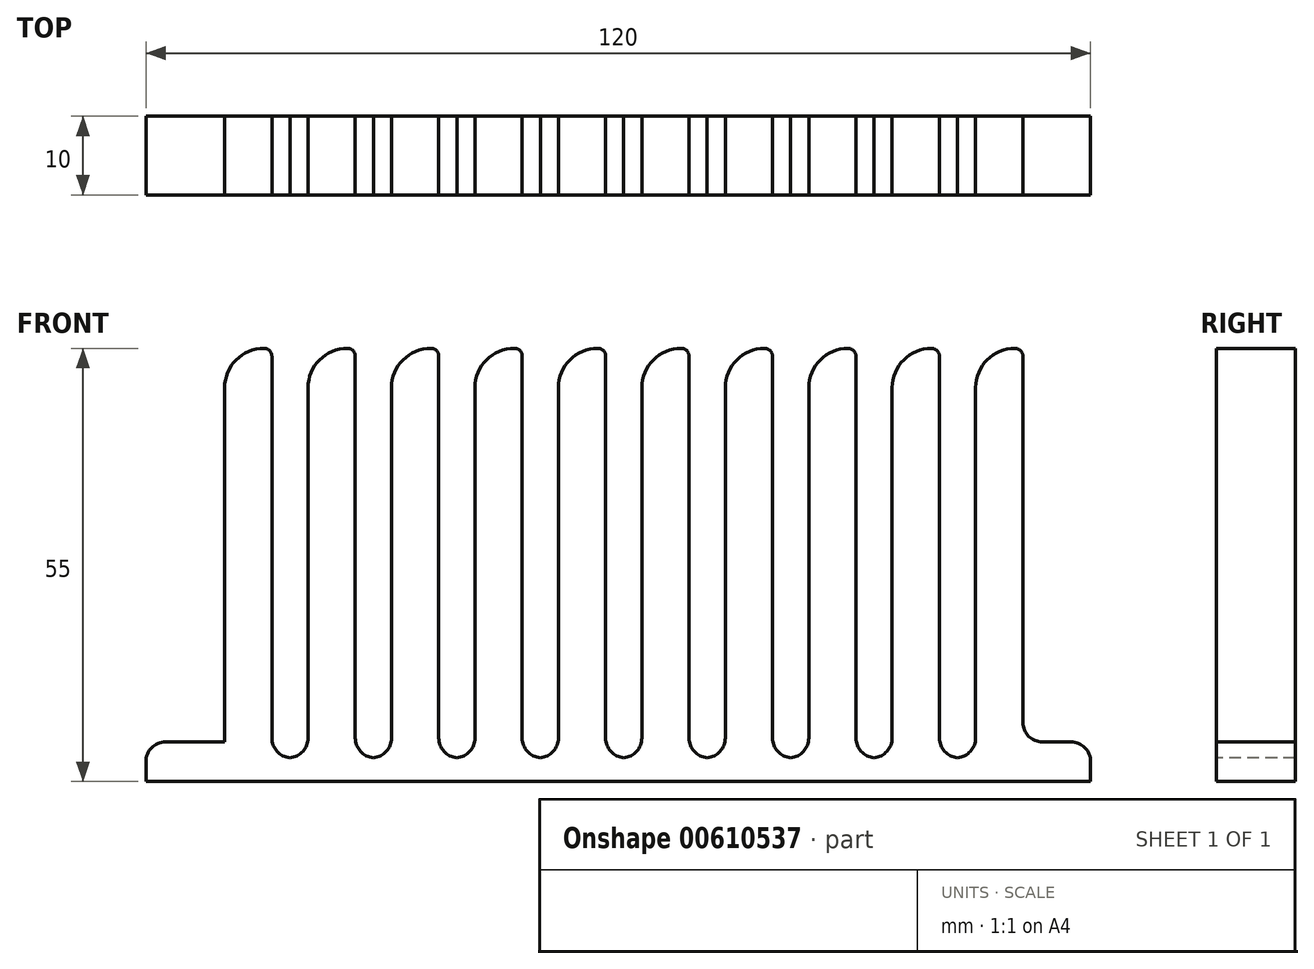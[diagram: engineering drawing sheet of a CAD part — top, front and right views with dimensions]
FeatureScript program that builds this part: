
annotation { "Feature Type Name" : "Feature", "Feature Type Description" : "" }
export const myFeature = defineFeature(function(context is Context, id is Id, definition is map)
    precondition{}
    {
        {
            var Q0;
            Q0=qCreatedBy(makeId("Top.planeOp"),FACE);
            var sketch = newSketch(context, id + "F0", { "sketchPlane" : qUnion([Q0])});
            skLineSegment(sketch, "E0.bottom", {"start": v(-61.1, -50) * mm, "end": v(58.9, -50) * mm});
            skLineSegment(sketch, "E0.top", {"start": v(-61.1, -60) * mm, "end": v(58.9, -60) * mm});
            skLineSegment(sketch, "E0.left", {"start": v(-61.1, -50) * mm, "end": v(-61.1, -60) * mm});
            skLineSegment(sketch, "E0.right", {"start": v(58.9, -50) * mm, "end": v(58.9, -60) * mm});
            skSolve(sketch);
        }
        {
            var Q0;
            Q0 = qSketchRegion(id + "F0", true);
            extrude(context, id + "F1", {"entities" : qUnion([Q0]), "depth" : 5 * mm, "offsetDistance" : 25 * mm});
        }
        {
            var Q0;
            Q0=makeQuery(id+"F1.opExtrude","CAP_FACE",FACE,{"disambiguationData":[OSD([sQuery(id+"F0.wireOp",EDGE,"E0.bottom"),sQuery(id+"F0.wireOp",EDGE,"E0.top"),sQuery(id+"F0.wireOp",EDGE,"E0.left"),sQuery(id+"F0.wireOp",EDGE,"E0.right")])],"isStart":false});
            var sketch = newSketch(context, id + "F2", { "sketchPlane" : qUnion([Q0])});
            skLineSegment(sketch, "E1.bottom", {"start": v(-51.1, -50) * mm, "end": v(-45.1, -50) * mm});
            skLineSegment(sketch, "E1.top", {"start": v(-51.1, -60) * mm, "end": v(-45.1, -60) * mm});
            skLineSegment(sketch, "E1.left", {"start": v(-51.1, -50) * mm, "end": v(-51.1, -60) * mm});
            skLineSegment(sketch, "E1.right", {"start": v(-45.1, -50) * mm, "end": v(-45.1, -60) * mm});
            skLineSegment(sketch, "E2.1.0.0", {"start": v(-34.5, -50) * mm, "end": v(-34.5, -60) * mm});
            skLineSegment(sketch, "E2.1.0.1", {"start": v(-40.5, -50) * mm, "end": v(-34.5, -50) * mm});
            skLineSegment(sketch, "E2.1.0.2", {"start": v(-40.5, -60) * mm, "end": v(-34.5, -60) * mm});
            skLineSegment(sketch, "E2.1.0.3", {"start": v(-40.5, -50) * mm, "end": v(-40.5, -60) * mm});
            skLineSegment(sketch, "E2.2.0.0", {"start": v(-23.9, -50) * mm, "end": v(-23.9, -60) * mm});
            skLineSegment(sketch, "E2.2.0.1", {"start": v(-29.9, -50) * mm, "end": v(-23.9, -50) * mm});
            skLineSegment(sketch, "E2.2.0.2", {"start": v(-29.9, -60) * mm, "end": v(-23.9, -60) * mm});
            skLineSegment(sketch, "E2.2.0.3", {"start": v(-29.9, -50) * mm, "end": v(-29.9, -60) * mm});
            skLineSegment(sketch, "E2.3.0.0", {"start": v(-13.3, -50) * mm, "end": v(-13.3, -60) * mm});
            skLineSegment(sketch, "E2.3.0.1", {"start": v(-19.3, -50) * mm, "end": v(-13.3, -50) * mm});
            skLineSegment(sketch, "E2.3.0.2", {"start": v(-19.3, -60) * mm, "end": v(-13.3, -60) * mm});
            skLineSegment(sketch, "E2.3.0.3", {"start": v(-19.3, -50) * mm, "end": v(-19.3, -60) * mm});
            skLineSegment(sketch, "E2.4.0.0", {"start": v(-2.7, -50) * mm, "end": v(-2.7, -60) * mm});
            skLineSegment(sketch, "E2.4.0.1", {"start": v(-8.7, -50) * mm, "end": v(-2.7, -50) * mm});
            skLineSegment(sketch, "E2.4.0.2", {"start": v(-8.7, -60) * mm, "end": v(-2.7, -60) * mm});
            skLineSegment(sketch, "E2.4.0.3", {"start": v(-8.7, -50) * mm, "end": v(-8.7, -60) * mm});
            skLineSegment(sketch, "E2.5.0.0", {"start": v(7.9, -50) * mm, "end": v(7.9, -60) * mm});
            skLineSegment(sketch, "E2.5.0.1", {"start": v(1.9, -50) * mm, "end": v(7.9, -50) * mm});
            skLineSegment(sketch, "E2.5.0.2", {"start": v(1.9, -60) * mm, "end": v(7.9, -60) * mm});
            skLineSegment(sketch, "E2.5.0.3", {"start": v(1.9, -50) * mm, "end": v(1.9, -60) * mm});
            skLineSegment(sketch, "E2.6.0.0", {"start": v(18.5, -50) * mm, "end": v(18.5, -60) * mm});
            skLineSegment(sketch, "E2.6.0.1", {"start": v(12.5, -50) * mm, "end": v(18.5, -50) * mm});
            skLineSegment(sketch, "E2.6.0.2", {"start": v(12.5, -60) * mm, "end": v(18.5, -60) * mm});
            skLineSegment(sketch, "E2.6.0.3", {"start": v(12.5, -50) * mm, "end": v(12.5, -60) * mm});
            skLineSegment(sketch, "E2.7.0.0", {"start": v(29.1, -50) * mm, "end": v(29.1, -60) * mm});
            skLineSegment(sketch, "E2.7.0.1", {"start": v(23.1, -50) * mm, "end": v(29.1, -50) * mm});
            skLineSegment(sketch, "E2.7.0.2", {"start": v(23.1, -60) * mm, "end": v(29.1, -60) * mm});
            skLineSegment(sketch, "E2.7.0.3", {"start": v(23.1, -50) * mm, "end": v(23.1, -60) * mm});
            skLineSegment(sketch, "E2.8.0.0", {"start": v(39.7, -50) * mm, "end": v(39.7, -60) * mm});
            skLineSegment(sketch, "E2.8.0.1", {"start": v(33.7, -50) * mm, "end": v(39.7, -50) * mm});
            skLineSegment(sketch, "E2.8.0.2", {"start": v(33.7, -60) * mm, "end": v(39.7, -60) * mm});
            skLineSegment(sketch, "E2.8.0.3", {"start": v(33.7, -50) * mm, "end": v(33.7, -60) * mm});
            skLineSegment(sketch, "E2.9.0.0", {"start": v(50.3, -50) * mm, "end": v(50.3, -60) * mm});
            skLineSegment(sketch, "E2.9.0.1", {"start": v(44.3, -50) * mm, "end": v(50.3, -50) * mm});
            skLineSegment(sketch, "E2.9.0.2", {"start": v(44.3, -60) * mm, "end": v(50.3, -60) * mm});
            skLineSegment(sketch, "E2.9.0.3", {"start": v(44.3, -50) * mm, "end": v(44.3, -60) * mm});
            skLineSegment(sketch, "E2.direction1", {"start": v(-51.1, -60) * mm, "end": v(-40.5, -60) * mm, "construction": true});
            skSolve(sketch);
        }
        {
            var Q0;
            Q0 = qSketchRegion(id + "F2", true);
            extrude(context, id + "F3", {"entities" : qUnion([Q0]), "operationType" : NewBodyOperationType.ADD, "depth" : 50 * mm, "offsetDistance" : 25 * mm});
        }
        {
            var Q0;
            {var subQ0=sQuery(id+"F0.wireOp",EDGE,"E0.top");var subQ1=sQuery(id+"F0.wireOp",EDGE,"E0.bottom");Q0=makeQuery(id+"F3.boolean.opBoolean","SPLIT",FACE,{"disambiguationData":[TD([makeQuery(id+"F3.opExtrude","SWEPT_FACE",FACE,{"disambiguationData":[OSD([sQuery(id+"F2.wireOp",EDGE,"E1.right")])]})])],"derivedFrom":makeQuery(id+"F1.opExtrude","CAP_FACE",FACE,{"disambiguationData":[OSD([subQ1,subQ0,sQuery(id+"F0.wireOp",EDGE,"E0.left"),sQuery(id+"F0.wireOp",EDGE,"E0.right")])],"isStart":false})});}
            var sketch = newSketch(context, id + "F4", { "sketchPlane" : qUnion([Q0])});
            skLineSegment(sketch, "E3.bottom", {"start": v(-45.1, -50) * mm, "end": v(-40.5, -50) * mm});
            skLineSegment(sketch, "E3.top", {"start": v(-45.1, -60) * mm, "end": v(-40.5, -60) * mm});
            skLineSegment(sketch, "E3.left", {"start": v(-45.1, -50) * mm, "end": v(-45.1, -60) * mm});
            skLineSegment(sketch, "E3.right", {"start": v(-40.5, -50) * mm, "end": v(-40.5, -60) * mm});
            skLineSegment(sketch, "E4.1.0.0", {"start": v(-34.5, -60) * mm, "end": v(-29.9, -60) * mm});
            skLineSegment(sketch, "E4.1.0.1", {"start": v(-34.5, -50) * mm, "end": v(-34.5, -60) * mm});
            skLineSegment(sketch, "E4.1.0.2", {"start": v(-29.9, -50) * mm, "end": v(-29.9, -60) * mm});
            skLineSegment(sketch, "E4.1.0.3", {"start": v(-34.5, -50) * mm, "end": v(-29.9, -50) * mm});
            skLineSegment(sketch, "E4.2.0.0", {"start": v(-23.9, -60) * mm, "end": v(-19.3, -60) * mm});
            skLineSegment(sketch, "E4.2.0.1", {"start": v(-23.9, -50) * mm, "end": v(-23.9, -60) * mm});
            skLineSegment(sketch, "E4.2.0.2", {"start": v(-19.3, -50) * mm, "end": v(-19.3, -60) * mm});
            skLineSegment(sketch, "E4.2.0.3", {"start": v(-23.9, -50) * mm, "end": v(-19.3, -50) * mm});
            skLineSegment(sketch, "E4.3.0.0", {"start": v(-13.3, -60) * mm, "end": v(-8.7, -60) * mm});
            skLineSegment(sketch, "E4.3.0.1", {"start": v(-13.3, -50) * mm, "end": v(-13.3, -60) * mm});
            skLineSegment(sketch, "E4.3.0.2", {"start": v(-8.7, -50) * mm, "end": v(-8.7, -60) * mm});
            skLineSegment(sketch, "E4.3.0.3", {"start": v(-13.3, -50) * mm, "end": v(-8.7, -50) * mm});
            skLineSegment(sketch, "E4.4.0.0", {"start": v(-2.7, -60) * mm, "end": v(1.9, -60) * mm});
            skLineSegment(sketch, "E4.4.0.1", {"start": v(-2.7, -50) * mm, "end": v(-2.7, -60) * mm});
            skLineSegment(sketch, "E4.4.0.2", {"start": v(1.9, -50) * mm, "end": v(1.9, -60) * mm});
            skLineSegment(sketch, "E4.4.0.3", {"start": v(-2.7, -50) * mm, "end": v(1.9, -50) * mm});
            skLineSegment(sketch, "E4.5.0.0", {"start": v(7.9, -60) * mm, "end": v(12.5, -60) * mm});
            skLineSegment(sketch, "E4.5.0.1", {"start": v(7.9, -50) * mm, "end": v(7.9, -60) * mm});
            skLineSegment(sketch, "E4.5.0.2", {"start": v(12.5, -50) * mm, "end": v(12.5, -60) * mm});
            skLineSegment(sketch, "E4.5.0.3", {"start": v(7.9, -50) * mm, "end": v(12.5, -50) * mm});
            skLineSegment(sketch, "E4.6.0.0", {"start": v(18.5, -60) * mm, "end": v(23.1, -60) * mm});
            skLineSegment(sketch, "E4.6.0.1", {"start": v(18.5, -50) * mm, "end": v(18.5, -60) * mm});
            skLineSegment(sketch, "E4.6.0.2", {"start": v(23.1, -50) * mm, "end": v(23.1, -60) * mm});
            skLineSegment(sketch, "E4.6.0.3", {"start": v(18.5, -50) * mm, "end": v(23.1, -50) * mm});
            skLineSegment(sketch, "E4.7.0.0", {"start": v(29.1, -60) * mm, "end": v(33.7, -60) * mm});
            skLineSegment(sketch, "E4.7.0.1", {"start": v(29.1, -50) * mm, "end": v(29.1, -60) * mm});
            skLineSegment(sketch, "E4.7.0.2", {"start": v(33.7, -50) * mm, "end": v(33.7, -60) * mm});
            skLineSegment(sketch, "E4.7.0.3", {"start": v(29.1, -50) * mm, "end": v(33.7, -50) * mm});
            skLineSegment(sketch, "E4.8.0.0", {"start": v(39.7, -60) * mm, "end": v(44.3, -60) * mm});
            skLineSegment(sketch, "E4.8.0.1", {"start": v(39.7, -50) * mm, "end": v(39.7, -60) * mm});
            skLineSegment(sketch, "E4.8.0.2", {"start": v(44.3, -50) * mm, "end": v(44.3, -60) * mm});
            skLineSegment(sketch, "E4.8.0.3", {"start": v(39.7, -50) * mm, "end": v(44.3, -50) * mm});
            skLineSegment(sketch, "E4.direction1", {"start": v(-45.1, -60) * mm, "end": v(-34.5, -60) * mm, "construction": true});
            skSolve(sketch);
        }
        {
            var Q0;
            Q0 = qSketchRegion(id + "F4", true);
            extrude(context, id + "F5", {"entities" : qUnion([Q0]), "operationType" : NewBodyOperationType.REMOVE, "oppositeDirection" : true, "depth" : 2 * mm, "offsetDistance" : 25 * mm});
        }
        {
            var Q0;
            Q0=makeQuery(id+"F5.boolean.opBoolean","COPY",EDGE,{"derivedFrom":makeQuery(id+"F5.opExtrude","CAP_EDGE",EDGE,{"disambiguationData":[OSD([sQuery(id+"F4.wireOp",EDGE,"E3.left")])],"isStart":false})});
            var Q1;
            Q1=makeQuery(id+"F5.boolean.opBoolean","COPY",EDGE,{"derivedFrom":makeQuery(id+"F5.opExtrude","CAP_EDGE",EDGE,{"disambiguationData":[OSD([sQuery(id+"F4.wireOp",EDGE,"E3.right")])],"isStart":false})});
            var Q2;
            Q2=makeQuery(id+"F5.boolean.opBoolean","COPY",EDGE,{"derivedFrom":makeQuery(id+"F5.opExtrude","CAP_EDGE",EDGE,{"disambiguationData":[OSD([sQuery(id+"F4.wireOp",EDGE,"E4.1.0.2")])],"isStart":false})});
            var Q3;
            Q3=makeQuery(id+"F5.boolean.opBoolean","COPY",EDGE,{"derivedFrom":makeQuery(id+"F5.opExtrude","CAP_EDGE",EDGE,{"disambiguationData":[OSD([sQuery(id+"F4.wireOp",EDGE,"E4.2.0.1")])],"isStart":false})});
            var Q4;
            Q4=makeQuery(id+"F5.boolean.opBoolean","COPY",EDGE,{"derivedFrom":makeQuery(id+"F5.opExtrude","CAP_EDGE",EDGE,{"disambiguationData":[OSD([sQuery(id+"F4.wireOp",EDGE,"E4.2.0.2")])],"isStart":false})});
            var Q5;
            Q5=makeQuery(id+"F5.boolean.opBoolean","COPY",EDGE,{"derivedFrom":makeQuery(id+"F5.opExtrude","CAP_EDGE",EDGE,{"disambiguationData":[OSD([sQuery(id+"F4.wireOp",EDGE,"E4.3.0.1")])],"isStart":false})});
            var Q6;
            Q6=makeQuery(id+"F5.boolean.opBoolean","COPY",EDGE,{"derivedFrom":makeQuery(id+"F5.opExtrude","CAP_EDGE",EDGE,{"disambiguationData":[OSD([sQuery(id+"F4.wireOp",EDGE,"E4.3.0.2")])],"isStart":false})});
            var Q7;
            Q7=makeQuery(id+"F5.boolean.opBoolean","COPY",EDGE,{"derivedFrom":makeQuery(id+"F5.opExtrude","CAP_EDGE",EDGE,{"disambiguationData":[OSD([sQuery(id+"F4.wireOp",EDGE,"E4.4.0.1")])],"isStart":false})});
            var Q8;
            Q8=makeQuery(id+"F5.boolean.opBoolean","COPY",EDGE,{"derivedFrom":makeQuery(id+"F5.opExtrude","CAP_EDGE",EDGE,{"disambiguationData":[OSD([sQuery(id+"F4.wireOp",EDGE,"E4.4.0.2")])],"isStart":false})});
            var Q9;
            Q9=makeQuery(id+"F5.boolean.opBoolean","COPY",EDGE,{"derivedFrom":makeQuery(id+"F5.opExtrude","CAP_EDGE",EDGE,{"disambiguationData":[OSD([sQuery(id+"F4.wireOp",EDGE,"E4.5.0.2")])],"isStart":false})});
            var Q10;
            Q10=makeQuery(id+"F5.boolean.opBoolean","COPY",EDGE,{"derivedFrom":makeQuery(id+"F5.opExtrude","CAP_EDGE",EDGE,{"disambiguationData":[OSD([sQuery(id+"F4.wireOp",EDGE,"E4.6.0.2")])],"isStart":false})});
            var Q11;
            Q11=makeQuery(id+"F5.boolean.opBoolean","COPY",EDGE,{"derivedFrom":makeQuery(id+"F5.opExtrude","CAP_EDGE",EDGE,{"disambiguationData":[OSD([sQuery(id+"F4.wireOp",EDGE,"E4.7.0.2")])],"isStart":false})});
            var Q12;
            Q12=makeQuery(id+"F5.boolean.opBoolean","COPY",EDGE,{"derivedFrom":makeQuery(id+"F5.opExtrude","CAP_EDGE",EDGE,{"disambiguationData":[OSD([sQuery(id+"F4.wireOp",EDGE,"E4.8.0.2")])],"isStart":false})});
            var Q13;
            Q13=makeQuery(id+"F5.boolean.opBoolean","COPY",EDGE,{"derivedFrom":makeQuery(id+"F5.opExtrude","CAP_EDGE",EDGE,{"disambiguationData":[OSD([sQuery(id+"F4.wireOp",EDGE,"E4.8.0.1")])],"isStart":false})});
            var Q14;
            Q14=makeQuery(id+"F5.boolean.opBoolean","COPY",EDGE,{"derivedFrom":makeQuery(id+"F5.opExtrude","CAP_EDGE",EDGE,{"disambiguationData":[OSD([sQuery(id+"F4.wireOp",EDGE,"E4.7.0.1")])],"isStart":false})});
            var Q15;
            Q15=makeQuery(id+"F5.boolean.opBoolean","COPY",EDGE,{"derivedFrom":makeQuery(id+"F5.opExtrude","CAP_EDGE",EDGE,{"disambiguationData":[OSD([sQuery(id+"F4.wireOp",EDGE,"E4.6.0.1")])],"isStart":false})});
            var Q16;
            Q16=makeQuery(id+"F5.boolean.opBoolean","COPY",EDGE,{"derivedFrom":makeQuery(id+"F5.opExtrude","CAP_EDGE",EDGE,{"disambiguationData":[OSD([sQuery(id+"F4.wireOp",EDGE,"E4.5.0.1")])],"isStart":false})});
            var Q17;
            Q17=makeQuery(id+"F3.opExtrude","CAP_EDGE",EDGE,{"disambiguationData":[OSD([sQuery(id+"F2.wireOp",EDGE,"E2.9.0.0")])],"isStart":true});
            var Q18;
            Q18=makeQuery(id+"F3.opExtrude","CAP_EDGE",EDGE,{"disambiguationData":[OSD([sQuery(id+"F2.wireOp",EDGE,"E1.left")])],"isStart":true});
            var Q19;
            Q19=makeQuery(id+"F5.boolean.opBoolean","COPY",EDGE,{"derivedFrom":makeQuery(id+"F5.opExtrude","CAP_EDGE",EDGE,{"disambiguationData":[OSD([sQuery(id+"F4.wireOp",EDGE,"E4.1.0.1")])],"isStart":false})});
            var Q20;
            Q20=makeQuery(id+"F1.opExtrude","CAP_EDGE",EDGE,{"disambiguationData":[OSD([sQuery(id+"F0.wireOp",EDGE,"E0.right")])],"isStart":false});
            var Q21;
            Q21=makeQuery(id+"F1.opExtrude","CAP_EDGE",EDGE,{"disambiguationData":[OSD([sQuery(id+"F0.wireOp",EDGE,"E0.left")])],"isStart":false});
            fillet(context, id + "F6", {"entities" : qUnion([Q0, Q1, Q2, Q3, Q4, Q5, Q6, Q7, Q8, Q9, Q10, Q11, Q12, Q13, Q14, Q15, Q16, Q17, Q18, Q19, Q20, Q21]), "radius" : 2.5 * mm, "tangentPropagation" : true, "allowEdgeOverflow" : false});
        }
        {
            var Q0;
            Q0=makeQuery(id+"F3.opExtrude","CAP_EDGE",EDGE,{"disambiguationData":[OSD([sQuery(id+"F2.wireOp",EDGE,"E1.left")])],"isStart":false});
            var Q1;
            Q1=makeQuery(id+"F3.opExtrude","CAP_EDGE",EDGE,{"disambiguationData":[OSD([sQuery(id+"F2.wireOp",EDGE,"E2.1.0.3")])],"isStart":false});
            var Q2;
            Q2=makeQuery(id+"F3.opExtrude","CAP_EDGE",EDGE,{"disambiguationData":[OSD([sQuery(id+"F2.wireOp",EDGE,"E2.2.0.3")])],"isStart":false});
            var Q3;
            Q3=makeQuery(id+"F3.opExtrude","CAP_EDGE",EDGE,{"disambiguationData":[OSD([sQuery(id+"F2.wireOp",EDGE,"E2.3.0.3")])],"isStart":false});
            var Q4;
            Q4=makeQuery(id+"F3.opExtrude","CAP_EDGE",EDGE,{"disambiguationData":[OSD([sQuery(id+"F2.wireOp",EDGE,"E2.4.0.3")])],"isStart":false});
            var Q5;
            Q5=makeQuery(id+"F3.opExtrude","CAP_EDGE",EDGE,{"disambiguationData":[OSD([sQuery(id+"F2.wireOp",EDGE,"E2.5.0.3")])],"isStart":false});
            var Q6;
            Q6=makeQuery(id+"F3.opExtrude","CAP_EDGE",EDGE,{"disambiguationData":[OSD([sQuery(id+"F2.wireOp",EDGE,"E2.6.0.3")])],"isStart":false});
            var Q7;
            Q7=makeQuery(id+"F3.opExtrude","CAP_EDGE",EDGE,{"disambiguationData":[OSD([sQuery(id+"F2.wireOp",EDGE,"E2.7.0.3")])],"isStart":false});
            var Q8;
            Q8=makeQuery(id+"F3.opExtrude","CAP_EDGE",EDGE,{"disambiguationData":[OSD([sQuery(id+"F2.wireOp",EDGE,"E2.8.0.3")])],"isStart":false});
            var Q9;
            Q9=makeQuery(id+"F3.opExtrude","CAP_EDGE",EDGE,{"disambiguationData":[OSD([sQuery(id+"F2.wireOp",EDGE,"E2.9.0.3")])],"isStart":false});
            fillet(context, id + "F7", {"entities" : qUnion([Q0, Q1, Q2, Q3, Q4, Q5, Q6, Q7, Q8, Q9]), "radius" : 5 * mm, "tangentPropagation" : true, "allowEdgeOverflow" : false});
        }
        {
            var Q0;
            Q0=makeQuery(id+"F3.opExtrude","CAP_EDGE",EDGE,{"disambiguationData":[OSD([sQuery(id+"F2.wireOp",EDGE,"E1.right")])],"isStart":false});
            var Q1;
            Q1=makeQuery(id+"F3.opExtrude","CAP_EDGE",EDGE,{"disambiguationData":[OSD([sQuery(id+"F2.wireOp",EDGE,"E2.1.0.0")])],"isStart":false});
            var Q2;
            Q2=makeQuery(id+"F3.opExtrude","CAP_EDGE",EDGE,{"disambiguationData":[OSD([sQuery(id+"F2.wireOp",EDGE,"E2.2.0.0")])],"isStart":false});
            var Q3;
            Q3=makeQuery(id+"F3.opExtrude","CAP_EDGE",EDGE,{"disambiguationData":[OSD([sQuery(id+"F2.wireOp",EDGE,"E2.3.0.0")])],"isStart":false});
            var Q4;
            Q4=makeQuery(id+"F3.opExtrude","CAP_EDGE",EDGE,{"disambiguationData":[OSD([sQuery(id+"F2.wireOp",EDGE,"E2.4.0.0")])],"isStart":false});
            var Q5;
            Q5=makeQuery(id+"F3.opExtrude","CAP_EDGE",EDGE,{"disambiguationData":[OSD([sQuery(id+"F2.wireOp",EDGE,"E2.5.0.0")])],"isStart":false});
            var Q6;
            Q6=makeQuery(id+"F3.opExtrude","CAP_EDGE",EDGE,{"disambiguationData":[OSD([sQuery(id+"F2.wireOp",EDGE,"E2.6.0.0")])],"isStart":false});
            var Q7;
            Q7=makeQuery(id+"F3.opExtrude","CAP_EDGE",EDGE,{"disambiguationData":[OSD([sQuery(id+"F2.wireOp",EDGE,"E2.7.0.0")])],"isStart":false});
            var Q8;
            Q8=makeQuery(id+"F3.opExtrude","CAP_EDGE",EDGE,{"disambiguationData":[OSD([sQuery(id+"F2.wireOp",EDGE,"E2.8.0.0")])],"isStart":false});
            var Q9;
            Q9=makeQuery(id+"F3.opExtrude","CAP_EDGE",EDGE,{"disambiguationData":[OSD([sQuery(id+"F2.wireOp",EDGE,"E2.9.0.0")])],"isStart":false});
            fillet(context, id + "F8", {"entities" : qUnion([Q0, Q1, Q2, Q3, Q4, Q5, Q6, Q7, Q8, Q9]), "radius" : 1 * mm, "tangentPropagation" : true, "allowEdgeOverflow" : false});
        }
    });
